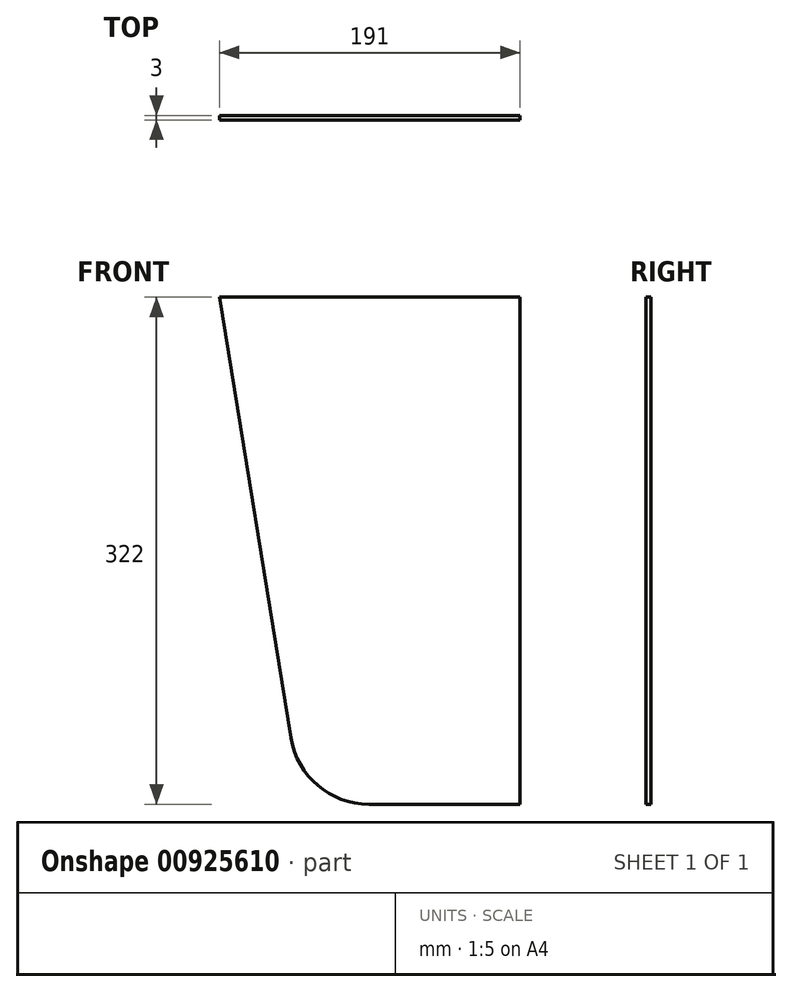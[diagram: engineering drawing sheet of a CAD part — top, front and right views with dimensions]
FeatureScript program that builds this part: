
annotation { "Feature Type Name" : "Feature", "Feature Type Description" : "" }
export const myFeature = defineFeature(function(context is Context, id is Id, definition is map)
    precondition{}
    {
        {
            var Q0;
            Q0=qCreatedBy(makeId("Front.planeOp"),FACE);
            var sketch = newSketch(context, id + "F0", { "sketchPlane" : qUnion([Q0])});
            skLineSegment(sketch, "E0", {"start": v(122.03, -135.8) * mm, "end": v(122.03, 186.2) * mm});
            skLineSegment(sketch, "E1", {"start": v(122.03, 186.2) * mm, "end": v(-68.97, 186.2) * mm});
            skLineSegment(sketch, "E2", {"start": v(-68.97, 186.2) * mm, "end": v(-23.49, -93.81) * mm});
            skLineSegment(sketch, "E3", {"start": v(122.03, -135.8) * mm, "end": v(25.86, -135.8) * mm});
            skPoint(sketch, "E4.visualSharp", {"position": v(-16.67, -135.8) * mm});
            skArc(sketch, "E4.filletArc", {"start": v(-23.49, -93.81) * mm, "mid": v(-6.53, -123.88) * mm, "end": v(25.86, -135.8) * mm});
            skSolve(sketch);
        }
        {
            var Q0;
            Q0 = qSketchRegion(id + "F0", true);
            extrude(context, id + "F1", {"entities" : qUnion([Q0]), "depth" : 3 * mm, "offsetDistance" : 25 * mm});
        }
    });
